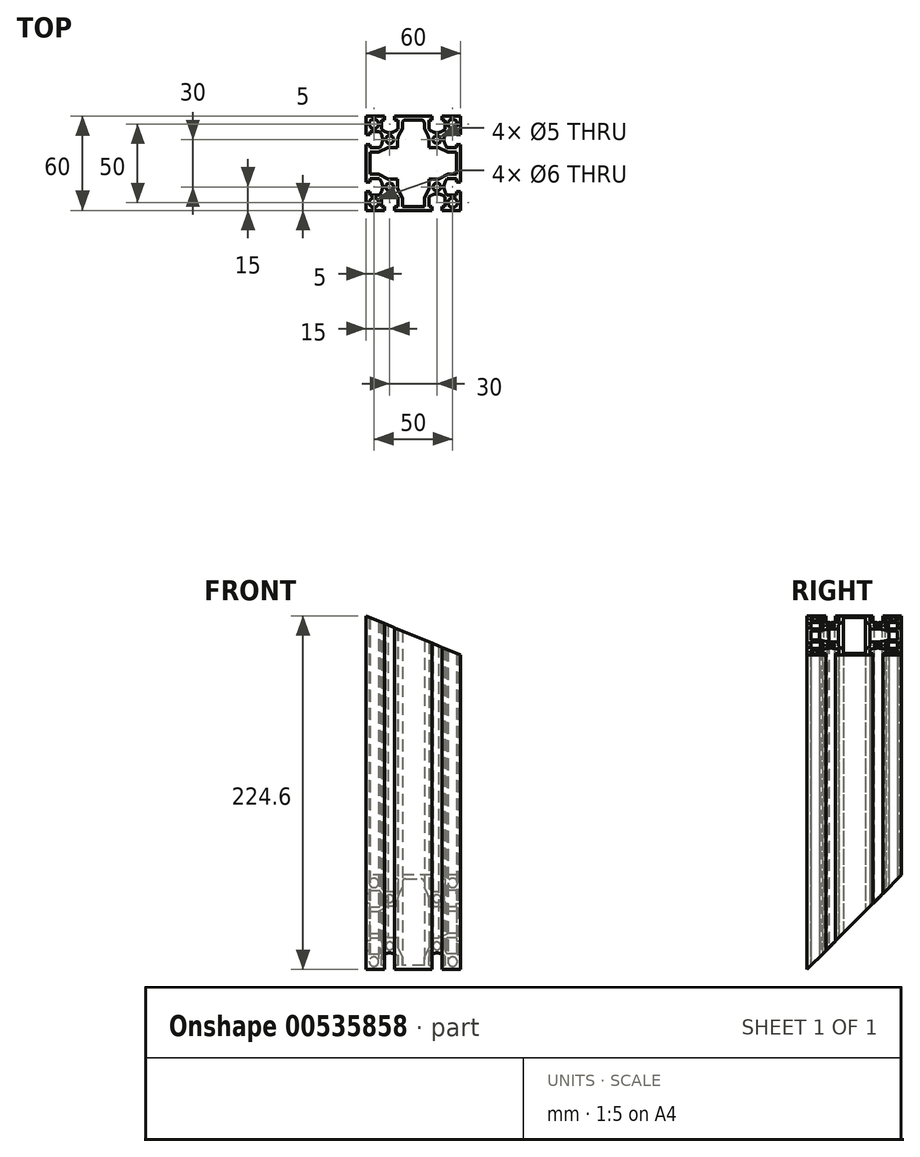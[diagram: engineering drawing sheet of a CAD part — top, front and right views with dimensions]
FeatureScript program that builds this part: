
annotation { "Feature Type Name" : "Feature", "Feature Type Description" : "" }
export const myFeature = defineFeature(function(context is Context, id is Id, definition is map)
    precondition{}
    {
        {
            var Q0;
            Q0=qCreatedBy(makeId("Top.planeOp"),FACE);
            var sketch = newSketch(context, id + "F0", { "sketchPlane" : qUnion([Q0])});
            skLineSegment(sketch, "E0.bottom", {"start": v(30, -30) * mm, "end": v(-30, -30) * mm});
            skLineSegment(sketch, "E0.top", {"start": v(30, 30) * mm, "end": v(-30, 30) * mm});
            skLineSegment(sketch, "E0.left", {"start": v(30, -30) * mm, "end": v(30, 30) * mm});
            skLineSegment(sketch, "E0.right", {"start": v(-30, -30) * mm, "end": v(-30, 30) * mm});
            skPoint(sketch, "E0.middle", {"position": v(0, 0) * mm});
            skLineSegment(sketch, "E1.top", {"start": v(-11.85, 30) * mm, "end": v(-18.15, 30) * mm});
            skLineSegment(sketch, "E1.left", {"start": v(-11.85, 27.5) * mm, "end": v(-11.85, 30) * mm});
            skLineSegment(sketch, "E1.right", {"start": v(-18.15, 27.5) * mm, "end": v(-18.15, 30) * mm});
            skPoint(sketch, "E1.middle", {"position": v(-15, 28.75) * mm});
            skLineSegment(sketch, "E2.bottom", {"start": v(-9.85, 27.5) * mm, "end": v(-11.85, 27.5) * mm});
            skLineSegment(sketch, "E2.left", {"start": v(-9.85, 27.5) * mm, "end": v(-9.85, 21.55) * mm});
            skLineSegment(sketch, "E2.right", {"start": v(-20.15, 27.5) * mm, "end": v(-20.15, 21.55) * mm});
            skPoint(sketch, "E2.middle", {"position": v(-15, 24.52) * mm});
            skArc(sketch, "E3", {"start": v(-20.15, 21.55) * mm, "mid": v(-15, 19.5) * mm, "end": v(-9.85, 21.55) * mm});
            skPoint(sketch, "E4.MirrorP", {"position": v(15, 24.52) * mm});
            skPoint(sketch, "E5.MirrorP", {"position": v(15, 28.75) * mm});
            skLineSegment(sketch, "E6.MirrorCS", {"start": v(11.85, 27.5) * mm, "end": v(11.85, 30) * mm});
            skLineSegment(sketch, "E7.MirrorCS", {"start": v(18.15, 27.5) * mm, "end": v(18.15, 30) * mm});
            skLineSegment(sketch, "E8.MirrorCS", {"start": v(9.85, 27.5) * mm, "end": v(11.85, 27.5) * mm});
            skLineSegment(sketch, "E9.MirrorCS", {"start": v(9.85, 27.5) * mm, "end": v(9.85, 21.55) * mm});
            skArc(sketch, "E10.MirrorCS", {"start": v(20.15, 21.55) * mm, "mid": v(15, 19.5) * mm, "end": v(9.85, 21.55) * mm});
            skLineSegment(sketch, "E11.MirrorCS", {"start": v(20.15, 27.5) * mm, "end": v(20.15, 21.55) * mm});
            skLineSegment(sketch, "E12.MirrorCS", {"start": v(11.85, 30) * mm, "end": v(18.15, 30) * mm});
            skLineSegment(sketch, "E13.1.0", {"start": v(27.5, 20.15) * mm, "end": v(21.55, 20.15) * mm});
            skLineSegment(sketch, "E13.1.1", {"start": v(27.5, 9.85) * mm, "end": v(21.55, 9.85) * mm});
            skArc(sketch, "E13.1.2", {"start": v(21.55, 20.15) * mm, "mid": v(19.5, 15) * mm, "end": v(21.55, 9.85) * mm});
            skLineSegment(sketch, "E13.1.3", {"start": v(27.5, -9.85) * mm, "end": v(21.55, -9.85) * mm});
            skLineSegment(sketch, "E13.1.4", {"start": v(27.5, -20.15) * mm, "end": v(21.55, -20.15) * mm});
            skPoint(sketch, "E13.1.5", {"position": v(28.75, 15) * mm});
            skPoint(sketch, "E13.1.6", {"position": v(28.75, -15) * mm});
            skArc(sketch, "E13.1.7", {"start": v(21.55, -20.15) * mm, "mid": v(19.5, -15) * mm, "end": v(21.55, -9.85) * mm});
            skPoint(sketch, "E13.1.8", {"position": v(24.52, -15) * mm});
            skPoint(sketch, "E13.1.9", {"position": v(24.52, 15) * mm});
            skLineSegment(sketch, "E13.1.10", {"start": v(27.5, 9.85) * mm, "end": v(27.5, 20.15) * mm});
            skLineSegment(sketch, "E13.1.11", {"start": v(27.5, -11.85) * mm, "end": v(27.5, -18.15) * mm});
            skLineSegment(sketch, "E13.1.12", {"start": v(30, 11.85) * mm, "end": v(30, 18.15) * mm});
            skLineSegment(sketch, "E13.1.13", {"start": v(30, -11.85) * mm, "end": v(30, -18.15) * mm});
            skLineSegment(sketch, "E13.1.14", {"start": v(27.5, 18.15) * mm, "end": v(30, 18.15) * mm});
            skLineSegment(sketch, "E13.1.15", {"start": v(27.5, 11.85) * mm, "end": v(30, 11.85) * mm});
            skLineSegment(sketch, "E13.1.16", {"start": v(27.5, 11.85) * mm, "end": v(27.5, 18.15) * mm});
            skLineSegment(sketch, "E13.1.17", {"start": v(27.5, -9.85) * mm, "end": v(27.5, -20.15) * mm});
            skLineSegment(sketch, "E13.1.18", {"start": v(27.5, -18.15) * mm, "end": v(30, -18.15) * mm});
            skLineSegment(sketch, "E13.1.19", {"start": v(27.5, -11.85) * mm, "end": v(30, -11.85) * mm});
            skLineSegment(sketch, "E13.2.0", {"start": v(20.15, -27.5) * mm, "end": v(20.15, -21.55) * mm});
            skLineSegment(sketch, "E13.2.1", {"start": v(9.85, -27.5) * mm, "end": v(9.85, -21.55) * mm});
            skArc(sketch, "E13.2.2", {"start": v(20.15, -21.55) * mm, "mid": v(15, -19.5) * mm, "end": v(9.85, -21.55) * mm});
            skLineSegment(sketch, "E13.2.3", {"start": v(-9.85, -27.5) * mm, "end": v(-9.85, -21.55) * mm});
            skLineSegment(sketch, "E13.2.4", {"start": v(-20.15, -27.5) * mm, "end": v(-20.15, -21.55) * mm});
            skPoint(sketch, "E13.2.5", {"position": v(15, -28.75) * mm});
            skPoint(sketch, "E13.2.6", {"position": v(-15, -28.75) * mm});
            skArc(sketch, "E13.2.7", {"start": v(-20.15, -21.55) * mm, "mid": v(-15, -19.5) * mm, "end": v(-9.85, -21.55) * mm});
            skPoint(sketch, "E13.2.8", {"position": v(-15, -24.52) * mm});
            skPoint(sketch, "E13.2.9", {"position": v(15, -24.52) * mm});
            skLineSegment(sketch, "E13.2.10", {"start": v(9.85, -27.5) * mm, "end": v(20.15, -27.5) * mm});
            skLineSegment(sketch, "E13.2.11", {"start": v(-11.85, -27.5) * mm, "end": v(-18.15, -27.5) * mm});
            skLineSegment(sketch, "E13.2.12", {"start": v(11.85, -30) * mm, "end": v(18.15, -30) * mm});
            skLineSegment(sketch, "E13.2.13", {"start": v(-11.85, -30) * mm, "end": v(-18.15, -30) * mm});
            skLineSegment(sketch, "E13.2.14", {"start": v(18.15, -27.5) * mm, "end": v(18.15, -30) * mm});
            skLineSegment(sketch, "E13.2.15", {"start": v(11.85, -27.5) * mm, "end": v(11.85, -30) * mm});
            skLineSegment(sketch, "E13.2.16", {"start": v(11.85, -27.5) * mm, "end": v(18.15, -27.5) * mm});
            skLineSegment(sketch, "E13.2.17", {"start": v(-9.85, -27.5) * mm, "end": v(-20.15, -27.5) * mm});
            skLineSegment(sketch, "E13.2.18", {"start": v(-18.15, -27.5) * mm, "end": v(-18.15, -30) * mm});
            skLineSegment(sketch, "E13.2.19", {"start": v(-11.85, -27.5) * mm, "end": v(-11.85, -30) * mm});
            skLineSegment(sketch, "E13.3.0", {"start": v(-27.5, -20.15) * mm, "end": v(-21.55, -20.15) * mm});
            skLineSegment(sketch, "E13.3.1", {"start": v(-27.5, -9.85) * mm, "end": v(-21.55, -9.85) * mm});
            skArc(sketch, "E13.3.2", {"start": v(-21.55, -20.15) * mm, "mid": v(-19.5, -15) * mm, "end": v(-21.55, -9.85) * mm});
            skLineSegment(sketch, "E13.3.3", {"start": v(-27.5, 9.85) * mm, "end": v(-21.55, 9.85) * mm});
            skLineSegment(sketch, "E13.3.4", {"start": v(-27.5, 20.15) * mm, "end": v(-21.55, 20.15) * mm});
            skPoint(sketch, "E13.3.5", {"position": v(-28.75, -15) * mm});
            skPoint(sketch, "E13.3.6", {"position": v(-28.75, 15) * mm});
            skArc(sketch, "E13.3.7", {"start": v(-21.55, 20.15) * mm, "mid": v(-19.5, 15) * mm, "end": v(-21.55, 9.85) * mm});
            skPoint(sketch, "E13.3.8", {"position": v(-24.52, 15) * mm});
            skPoint(sketch, "E13.3.9", {"position": v(-24.52, -15) * mm});
            skLineSegment(sketch, "E13.3.10", {"start": v(-27.5, -9.85) * mm, "end": v(-27.5, -20.15) * mm});
            skLineSegment(sketch, "E13.3.11", {"start": v(-27.5, 11.85) * mm, "end": v(-27.5, 18.15) * mm});
            skLineSegment(sketch, "E13.3.12", {"start": v(-30, -11.85) * mm, "end": v(-30, -18.15) * mm});
            skLineSegment(sketch, "E13.3.13", {"start": v(-30, 11.85) * mm, "end": v(-30, 18.15) * mm});
            skLineSegment(sketch, "E13.3.14", {"start": v(-27.5, -18.15) * mm, "end": v(-30, -18.15) * mm});
            skLineSegment(sketch, "E13.3.15", {"start": v(-27.5, -11.85) * mm, "end": v(-30, -11.85) * mm});
            skLineSegment(sketch, "E13.3.16", {"start": v(-27.5, -11.85) * mm, "end": v(-27.5, -18.15) * mm});
            skLineSegment(sketch, "E13.3.17", {"start": v(-27.5, 9.85) * mm, "end": v(-27.5, 20.15) * mm});
            skLineSegment(sketch, "E13.3.18", {"start": v(-27.5, 18.15) * mm, "end": v(-30, 18.15) * mm});
            skLineSegment(sketch, "E13.3.19", {"start": v(-27.5, 11.85) * mm, "end": v(-30, 11.85) * mm});
            skLineSegment(sketch, "E13.anchor1", {"start": v(0, 0) * mm, "end": v(-20.15, 21.55) * mm, "construction": true});
            skLineSegment(sketch, "E13.anchor2", {"start": v(0, 0) * mm, "end": v(-21.55, -20.15) * mm, "construction": true});
            skLineSegment(sketch, "E14.trimOffspring", {"start": v(-18.15, 27.5) * mm, "end": v(-20.15, 27.5) * mm});
            skLineSegment(sketch, "E15.trimOffspring", {"start": v(18.15, 27.5) * mm, "end": v(20.15, 27.5) * mm});
            skCircle(sketch, "E16", {"center": v(-15, 15) * mm, "radius": 2.5 * mm});
            skCircle(sketch, "E17", {"center": v(-25, 25) * mm, "radius": 3 * mm});
            skCircle(sketch, "E18.MirrorC", {"center": v(25, 25) * mm, "radius": 3 * mm});
            skCircle(sketch, "E19.MirrorC", {"center": v(25, -25) * mm, "radius": 3 * mm});
            skCircle(sketch, "E20.MirrorC", {"center": v(-25, -25) * mm, "radius": 3 * mm});
            skCircle(sketch, "E21.MirrorC", {"center": v(15, 15) * mm, "radius": 2.5 * mm});
            skCircle(sketch, "E22.MirrorC", {"center": v(15, -15) * mm, "radius": 2.5 * mm});
            skCircle(sketch, "E23.MirrorC", {"center": v(-15, -15) * mm, "radius": 2.5 * mm});
            skLineSegment(sketch, "E24", {"start": v(-7, 27.5) * mm, "end": v(0, 27.5) * mm});
            skLineSegment(sketch, "E25", {"start": v(-7, 27.5) * mm, "end": v(-7, 22) * mm});
            skLineSegment(sketch, "E26", {"start": v(-10, 10) * mm, "end": v(-10, 16) * mm});
            skLineSegment(sketch, "E27", {"start": v(-10, 16) * mm, "end": v(-7, 22) * mm});
            skLineSegment(sketch, "E28.MirrorCS", {"start": v(10, 10) * mm, "end": v(10, 16) * mm});
            skLineSegment(sketch, "E29.MirrorCS", {"start": v(10, 16) * mm, "end": v(7, 22) * mm});
            skLineSegment(sketch, "E30.MirrorCS", {"start": v(7, 27.5) * mm, "end": v(0, 27.5) * mm});
            skLineSegment(sketch, "E31.MirrorCS", {"start": v(7, 27.5) * mm, "end": v(7, 22) * mm});
            skLineSegment(sketch, "E32.1.0", {"start": v(-10, -10) * mm, "end": v(-16, -10) * mm});
            skLineSegment(sketch, "E32.1.1", {"start": v(-16, -10) * mm, "end": v(-22, -7) * mm});
            skLineSegment(sketch, "E32.1.2", {"start": v(-27.5, -7) * mm, "end": v(-22, -7) * mm});
            skLineSegment(sketch, "E32.1.3", {"start": v(-27.5, -7) * mm, "end": v(-27.5, 0) * mm});
            skLineSegment(sketch, "E32.1.4", {"start": v(-27.5, 7) * mm, "end": v(-27.5, 0) * mm});
            skLineSegment(sketch, "E32.1.5", {"start": v(-27.5, 7) * mm, "end": v(-22, 7) * mm});
            skLineSegment(sketch, "E32.1.6", {"start": v(-16, 10) * mm, "end": v(-22, 7) * mm});
            skLineSegment(sketch, "E32.1.7", {"start": v(-10, 10) * mm, "end": v(-16, 10) * mm});
            skLineSegment(sketch, "E32.2.0", {"start": v(10, -10) * mm, "end": v(10, -16) * mm});
            skLineSegment(sketch, "E32.2.1", {"start": v(10, -16) * mm, "end": v(7, -22) * mm});
            skLineSegment(sketch, "E32.2.2", {"start": v(7, -27.5) * mm, "end": v(7, -22) * mm});
            skLineSegment(sketch, "E32.2.3", {"start": v(7, -27.5) * mm, "end": v(0, -27.5) * mm});
            skLineSegment(sketch, "E32.2.4", {"start": v(-7, -27.5) * mm, "end": v(0, -27.5) * mm});
            skLineSegment(sketch, "E32.2.5", {"start": v(-7, -27.5) * mm, "end": v(-7, -22) * mm});
            skLineSegment(sketch, "E32.2.6", {"start": v(-10, -16) * mm, "end": v(-7, -22) * mm});
            skLineSegment(sketch, "E32.2.7", {"start": v(-10, -10) * mm, "end": v(-10, -16) * mm});
            skLineSegment(sketch, "E32.3.0", {"start": v(10, 10) * mm, "end": v(16, 10) * mm});
            skLineSegment(sketch, "E32.3.1", {"start": v(16, 10) * mm, "end": v(22, 7) * mm});
            skLineSegment(sketch, "E32.3.2", {"start": v(27.5, 7) * mm, "end": v(22, 7) * mm});
            skLineSegment(sketch, "E32.3.3", {"start": v(27.5, 7) * mm, "end": v(27.5, 0) * mm});
            skLineSegment(sketch, "E32.3.4", {"start": v(27.5, -7) * mm, "end": v(27.5, 0) * mm});
            skLineSegment(sketch, "E32.3.5", {"start": v(27.5, -7) * mm, "end": v(22, -7) * mm});
            skLineSegment(sketch, "E32.3.6", {"start": v(16, -10) * mm, "end": v(22, -7) * mm});
            skLineSegment(sketch, "E32.3.7", {"start": v(10, -10) * mm, "end": v(16, -10) * mm});
            skSolve(sketch);
        }
        {
            var Q0;
            {var subQ30=sQuery(id+"F0.wireOp",EDGE,"E1.left");Q0=makeQuery(id+"F0.imprint","IMPRINT",FACE,{"disambiguationData":[TD([[makeQuery(id+"F0.imprint","IMPRINT",EDGE,{"derivedFrom":subQ30}),-1.0]])]});}
            extrude(context, id + "F1", {"entities" : qUnion([Q0]), "depth" : 224.6 * mm, "offsetDistance" : 25 * mm});
        }
        {
            var Q0;
            Q0=makeQuery(id+"F1.opExtrude","SWEPT_EDGE",EDGE,{"disambiguationData":[OSD([sQuery(id+"F0.wireOp",EDGE,"E24"),sQuery(id+"F0.wireOp",EDGE,"E25")])]});
            var Q1;
            Q1=makeQuery(id+"F1.opExtrude","SWEPT_EDGE",EDGE,{"disambiguationData":[OSD([sQuery(id+"F0.wireOp",EDGE,"E30.MirrorCS"),sQuery(id+"F0.wireOp",EDGE,"E31.MirrorCS")])]});
            var Q2;
            Q2=makeQuery(id+"F1.opExtrude","SWEPT_EDGE",EDGE,{"disambiguationData":[OSD([sQuery(id+"F0.wireOp",EDGE,"840db5bc-c403-45cd-90c7-254e62d9e8c5.3.2"),sQuery(id+"F0.wireOp",EDGE,"840db5bc-c403-45cd-90c7-254e62d9e8c5.3.3")])]});
            var Q3;
            Q3=makeQuery(id+"F1.opExtrude","SWEPT_EDGE",EDGE,{"disambiguationData":[OSD([sQuery(id+"F0.wireOp",EDGE,"840db5bc-c403-45cd-90c7-254e62d9e8c5.3.4"),sQuery(id+"F0.wireOp",EDGE,"840db5bc-c403-45cd-90c7-254e62d9e8c5.3.5")])]});
            var Q4;
            Q4=makeQuery(id+"F1.opExtrude","SWEPT_EDGE",EDGE,{"disambiguationData":[OSD([sQuery(id+"F0.wireOp",EDGE,"840db5bc-c403-45cd-90c7-254e62d9e8c5.1.4"),sQuery(id+"F0.wireOp",EDGE,"840db5bc-c403-45cd-90c7-254e62d9e8c5.1.5")])]});
            var Q5;
            Q5=makeQuery(id+"F1.opExtrude","SWEPT_EDGE",EDGE,{"disambiguationData":[OSD([sQuery(id+"F0.wireOp",EDGE,"840db5bc-c403-45cd-90c7-254e62d9e8c5.1.2"),sQuery(id+"F0.wireOp",EDGE,"840db5bc-c403-45cd-90c7-254e62d9e8c5.1.3")])]});
            var Q6;
            Q6=makeQuery(id+"F1.opExtrude","SWEPT_EDGE",EDGE,{"disambiguationData":[OSD([sQuery(id+"F0.wireOp",EDGE,"840db5bc-c403-45cd-90c7-254e62d9e8c5.2.2"),sQuery(id+"F0.wireOp",EDGE,"840db5bc-c403-45cd-90c7-254e62d9e8c5.2.3")])]});
            var Q7;
            Q7=makeQuery(id+"F1.opExtrude","SWEPT_EDGE",EDGE,{"disambiguationData":[OSD([sQuery(id+"F0.wireOp",EDGE,"840db5bc-c403-45cd-90c7-254e62d9e8c5.2.4"),sQuery(id+"F0.wireOp",EDGE,"840db5bc-c403-45cd-90c7-254e62d9e8c5.2.5")])]});
            fillet(context, id + "F2", {"entities" : qUnion([Q0, Q1, Q2, Q3, Q4, Q5, Q6, Q7]), "radius" : 2 * mm, "tangentPropagation" : true, "allowEdgeOverflow" : false});
        }
        {
            var Q0;
            Q0=makeQuery(id+"F1.opExtrude","SWEPT_EDGE",EDGE,{"disambiguationData":[OSD([sQuery(id+"F0.wireOp",EDGE,"E26"),sQuery(id+"F0.wireOp",EDGE,"E27")])]});
            var Q1;
            Q1=makeQuery(id+"F1.opExtrude","SWEPT_EDGE",EDGE,{"disambiguationData":[OSD([sQuery(id+"F0.wireOp",EDGE,"E28.MirrorCS"),sQuery(id+"F0.wireOp",EDGE,"E29.MirrorCS")])]});
            var Q2;
            Q2=makeQuery(id+"F1.opExtrude","SWEPT_EDGE",EDGE,{"disambiguationData":[OSD([sQuery(id+"F0.wireOp",EDGE,"840db5bc-c403-45cd-90c7-254e62d9e8c5.3.0"),sQuery(id+"F0.wireOp",EDGE,"840db5bc-c403-45cd-90c7-254e62d9e8c5.3.1")])]});
            var Q3;
            Q3=makeQuery(id+"F1.opExtrude","SWEPT_EDGE",EDGE,{"disambiguationData":[OSD([sQuery(id+"F0.wireOp",EDGE,"840db5bc-c403-45cd-90c7-254e62d9e8c5.1.6"),sQuery(id+"F0.wireOp",EDGE,"840db5bc-c403-45cd-90c7-254e62d9e8c5.1.7")])]});
            var Q4;
            Q4=makeQuery(id+"F1.opExtrude","SWEPT_EDGE",EDGE,{"disambiguationData":[OSD([sQuery(id+"F0.wireOp",EDGE,"840db5bc-c403-45cd-90c7-254e62d9e8c5.1.0"),sQuery(id+"F0.wireOp",EDGE,"840db5bc-c403-45cd-90c7-254e62d9e8c5.1.1")])]});
            var Q5;
            Q5=makeQuery(id+"F1.opExtrude","SWEPT_EDGE",EDGE,{"disambiguationData":[OSD([sQuery(id+"F0.wireOp",EDGE,"840db5bc-c403-45cd-90c7-254e62d9e8c5.3.6"),sQuery(id+"F0.wireOp",EDGE,"840db5bc-c403-45cd-90c7-254e62d9e8c5.3.7")])]});
            var Q6;
            Q6=makeQuery(id+"F1.opExtrude","SWEPT_EDGE",EDGE,{"disambiguationData":[OSD([sQuery(id+"F0.wireOp",EDGE,"840db5bc-c403-45cd-90c7-254e62d9e8c5.2.0"),sQuery(id+"F0.wireOp",EDGE,"840db5bc-c403-45cd-90c7-254e62d9e8c5.2.1")])]});
            var Q7;
            Q7=makeQuery(id+"F1.opExtrude","SWEPT_EDGE",EDGE,{"disambiguationData":[OSD([sQuery(id+"F0.wireOp",EDGE,"840db5bc-c403-45cd-90c7-254e62d9e8c5.2.6"),sQuery(id+"F0.wireOp",EDGE,"840db5bc-c403-45cd-90c7-254e62d9e8c5.2.7")])]});
            fillet(context, id + "F3", {"entities" : qUnion([Q0, Q1, Q2, Q3, Q4, Q5, Q6, Q7]), "radius" : 7 * mm, "tangentPropagation" : true, "allowEdgeOverflow" : false});
        }
        {
            var Q0;
            {var subQ0=sQuery(id+"F0.wireOp",EDGE,"E0.bottom");Q0=makeQuery(id+"F1.opExtrude","SWEPT_FACE",FACE,{"disambiguationData":[OSD([subQ0]),TDD([makeQuery(id+"F0.imprint","IMPRINT",EDGE,{"disambiguationData":[TD([[makeQuery(id+"F0.imprint","INTERSECT",VERTEX,{"derivedFrom":[subQ0,sQuery(id+"F0.wireOp",EDGE,"E13.2.12"),sQuery(id+"F0.wireOp",EDGE,"E13.2.15")]}),-1.0]])],"derivedFrom":subQ0})])]});}
            var sketch = newSketch(context, id + "F4", { "sketchPlane" : qUnion([Q0])});
            skLineSegment(sketch, "E33.0", {"start": v(-18.15, 224.6) * mm, "end": v(-30, 224.6) * mm});
            skLineSegment(sketch, "E33.1", {"start": v(30, 224.6) * mm, "end": v(30, 0) * mm});
            skLineSegment(sketch, "E34", {"start": v(-30, 224.6) * mm, "end": v(30, 224.6) * mm});
            skLineSegment(sketch, "E35", {"start": v(30, 164.6) * mm, "end": v(-30, 224.6) * mm});
            skLineSegment(sketch, "E36.0", {"start": v(-18.15, 0) * mm, "end": v(-30, 0) * mm});
            skLineSegment(sketch, "E37", {"start": v(-30, 0) * mm, "end": v(30, 0) * mm});
            skLineSegment(sketch, "E38", {"start": v(30, 60) * mm, "end": v(-30, 0) * mm});
            skSolve(sketch);
        }
        {
            var Q0;
            Q0=qCreatedBy(makeId("Right.planeOp"),FACE);
            var sketch = newSketch(context, id + "F5", { "sketchPlane" : qUnion([Q0])});
            skLineSegment(sketch, "E39.bottom", {"start": v(211.64, 40.85) * mm, "end": v(111.25, 141.25) * mm});
            skLineSegment(sketch, "E39.top", {"start": v(70.4, -100.4) * mm, "end": v(-30, 0) * mm});
            skLineSegment(sketch, "E39.left", {"start": v(211.64, 40.85) * mm, "end": v(70.4, -100.4) * mm});
            skLineSegment(sketch, "E39.right", {"start": v(111.25, 141.25) * mm, "end": v(-30, 0) * mm});
            skSolve(sketch);
        }
        {
            var Q0;
            Q0 = qSketchRegion(id + "F5", true);
            extrude(context, id + "F6", {"entities" : qUnion([Q0]), "operationType" : NewBodyOperationType.REMOVE, "oppositeDirection" : true, "depth" : 30 * mm, "offsetDistance" : 25 * mm, "hasSecondDirection" : true, "secondDirectionOppositeDirection" : false, "secondDirectionDepth" : 30 * mm});
        }
        {
            var Q0;
            Q0=qCreatedBy(makeId("Front.planeOp"),FACE);
            var sketch = newSketch(context, id + "F7", { "sketchPlane" : qUnion([Q0])});
            skLineSegment(sketch, "E40.bottom", {"start": v(32.1, 374.51) * mm, "end": v(136.09, 331.44) * mm});
            skLineSegment(sketch, "E40.top", {"start": v(-30, 224.6) * mm, "end": v(74, 181.53) * mm});
            skLineSegment(sketch, "E40.left", {"start": v(32.1, 374.51) * mm, "end": v(-30, 224.6) * mm});
            skLineSegment(sketch, "E40.right", {"start": v(136.09, 331.44) * mm, "end": v(74, 181.53) * mm});
            skSolve(sketch);
        }
        {
            var Q0;
            Q0 = qSketchRegion(id + "F7", true);
            extrude(context, id + "F8", {"entities" : qUnion([Q0]), "operationType" : NewBodyOperationType.REMOVE, "depth" : 30 * mm, "offsetDistance" : 25 * mm, "hasSecondDirection" : true, "secondDirectionOppositeDirection" : true, "secondDirectionDepth" : 30 * mm});
        }
    });
